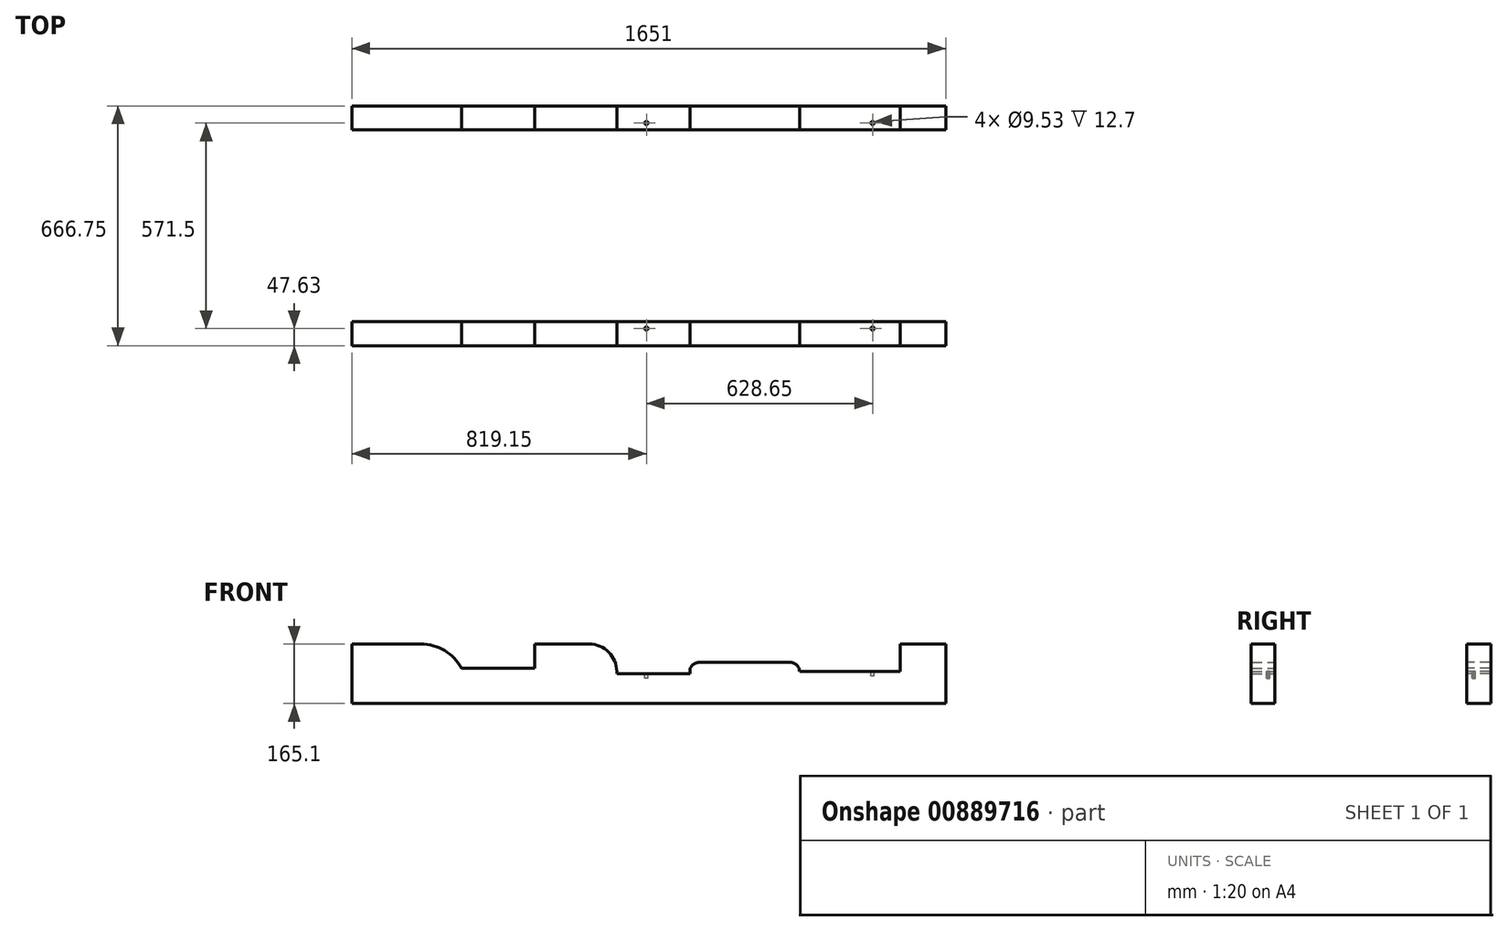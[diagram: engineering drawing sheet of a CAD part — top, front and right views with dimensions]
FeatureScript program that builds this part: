
annotation { "Feature Type Name" : "Feature", "Feature Type Description" : "" }
export const myFeature = defineFeature(function(context is Context, id is Id, definition is map)
    precondition{}
    {
        {
            var Q0;
            Q0=qCreatedBy(makeId("Front.planeOp"),FACE);
            var sketch = newSketch(context, id + "F0", { "sketchPlane" : qUnion([Q0])});
            skLineSegment(sketch, "E0", {"start": v(0, 0) * mm, "end": v(0, 165.1) * mm});
            skLineSegment(sketch, "E1", {"start": v(0, 165.1) * mm, "end": v(736.6, 165.1) * mm});
            skLineSegment(sketch, "E2", {"start": v(736.6, 165.1) * mm, "end": v(736.6, 82.55) * mm});
            skLineSegment(sketch, "E3", {"start": v(736.6, 82.55) * mm, "end": v(939.8, 82.55) * mm});
            skLineSegment(sketch, "E4", {"start": v(939.8, 82.55) * mm, "end": v(939.8, 114.3) * mm});
            skLineSegment(sketch, "E5", {"start": v(939.8, 114.3) * mm, "end": v(1244.6, 114.3) * mm});
            skLineSegment(sketch, "E6", {"start": v(1651, 165.1) * mm, "end": v(1651, 0) * mm});
            skLineSegment(sketch, "E7", {"start": v(1651, 0) * mm, "end": v(0, 0) * mm});
            skPoint(sketch, "E8.end.orphan", {"position": v(1244.6, 82.55) * mm});
            skLineSegment(sketch, "E9", {"start": v(1244.6, 114.3) * mm, "end": v(1244.6, 88.9) * mm});
            skLineSegment(sketch, "E10", {"start": v(1244.6, 88.9) * mm, "end": v(1524, 88.9) * mm});
            skLineSegment(sketch, "E11", {"start": v(1524, 88.9) * mm, "end": v(1524, 165.1) * mm});
            skLineSegment(sketch, "E12", {"start": v(1524, 165.1) * mm, "end": v(1651, 165.1) * mm});
            skSolve(sketch);
        }
        {
            var Q0;
            Q0=makeQuery(id+"F0.imprint","IMPRINT",FACE,{"disambiguationData":[TD([[makeQuery(id+"F0.imprint","IMPRINT",EDGE,{"derivedFrom":sQuery(id+"F0.wireOp",EDGE,"E0")}),-1.0]])]});
            extrude(context, id + "F1", {"entities" : qUnion([Q0]), "oppositeDirection" : true, "depth" : 66.67 * mm, "offsetDistance" : 25.4 * mm});
        }
        {
            var Q0;
            Q0=makeQuery(id+"F1.opExtrude","SWEPT_FACE",FACE,{"disambiguationData":[OSD([sQuery(id+"F0.wireOp",EDGE,"E3")])]});
            var sketch = newSketch(context, id + "F2", { "sketchPlane" : qUnion([Q0])});
            skLineSegment(sketch, "E13", {"start": v(736.6, 0) * mm, "end": v(819.15, 0) * mm, "construction": true});
            skLineSegment(sketch, "E14", {"start": v(819.15, 0) * mm, "end": v(819.15, 19.05) * mm, "construction": true});
            skCircle(sketch, "E15", {"center": v(819.15, 19.05) * mm, "radius": 4.76 * mm});
            skSolve(sketch);
        }
        {
            var Q0;
            Q0=makeQuery(id+"F2.imprint","IMPRINT",FACE,{"disambiguationData":[TD([[makeQuery(id+"F2.imprint","IMPRINT",EDGE,{"derivedFrom":sQuery(id+"F2.wireOp",EDGE,"E15")}),1.0]])]});
            extrude(context, id + "F3", {"entities" : qUnion([Q0]), "operationType" : NewBodyOperationType.REMOVE, "oppositeDirection" : true, "depth" : 12.7 * mm, "offsetDistance" : 25.4 * mm});
        }
        {
            var Q0;
            Q0=makeQuery(id+"F1.opExtrude","SWEPT_FACE",FACE,{"disambiguationData":[OSD([sQuery(id+"F0.wireOp",EDGE,"E10")])]});
            var sketch = newSketch(context, id + "F4", { "sketchPlane" : qUnion([Q0])});
            skLineSegment(sketch, "E16", {"start": v(1244.6, 0) * mm, "end": v(1447.8, 0) * mm, "construction": true});
            skLineSegment(sketch, "E17", {"start": v(1447.8, 0) * mm, "end": v(1447.8, 19.05) * mm, "construction": true});
            skCircle(sketch, "E18", {"center": v(1447.8, 19.05) * mm, "radius": 4.76 * mm});
            skSolve(sketch);
        }
        {
            var Q0;
            Q0 = qSketchRegion(id + "F4", true);
            extrude(context, id + "F5", {"entities" : qUnion([Q0]), "operationType" : NewBodyOperationType.REMOVE, "oppositeDirection" : true, "depth" : 12.7 * mm, "offsetDistance" : 25.4 * mm});
        }
        {
            var Q0;
            Q0=makeQuery(id+"F1.opExtrude","SWEPT_EDGE",EDGE,{"disambiguationData":[OSD([sQuery(id+"F0.wireOp",EDGE,"E1"),sQuery(id+"F0.wireOp",EDGE,"E2")])]});
            fillet(context, id + "F6", {"entities" : qUnion([Q0]), "radius" : 76.2 * mm, "tangentPropagation" : true, "allowEdgeOverflow" : false});
        }
        {
            var Q0;
            Q0=makeQuery(id+"F1.opExtrude","SWEPT_EDGE",EDGE,{"disambiguationData":[OSD([sQuery(id+"F0.wireOp",EDGE,"E4"),sQuery(id+"F0.wireOp",EDGE,"E5")])]});
            var Q1;
            Q1=makeQuery(id+"F1.opExtrude","SWEPT_EDGE",EDGE,{"disambiguationData":[OSD([sQuery(id+"F0.wireOp",EDGE,"E5"),sQuery(id+"F0.wireOp",EDGE,"E9")])]});
            fillet(context, id + "F7", {"entities" : qUnion([Q0, Q1]), "radius" : 25.4 * mm, "tangentPropagation" : true, "allowEdgeOverflow" : false});
        }
        {
            var Q0;
            Q0=makeQuery(id+"F1.opExtrude","CAP_FACE",FACE,{"disambiguationData":[OSD([sQuery(id+"F0.wireOp",EDGE,"E0"),sQuery(id+"F0.wireOp",EDGE,"E1"),sQuery(id+"F0.wireOp",EDGE,"E2"),sQuery(id+"F0.wireOp",EDGE,"E3"),sQuery(id+"F0.wireOp",EDGE,"E4"),sQuery(id+"F0.wireOp",EDGE,"E5"),sQuery(id+"F0.wireOp",EDGE,"E6"),sQuery(id+"F0.wireOp",EDGE,"E7"),sQuery(id+"F0.wireOp",EDGE,"E9"),sQuery(id+"F0.wireOp",EDGE,"E10"),sQuery(id+"F0.wireOp",EDGE,"E11"),sQuery(id+"F0.wireOp",EDGE,"E12")])],"isStart":true});
            cPlane(context, id + "F8", {"entities" : qUnion([Q0]), "cplaneType" : CPlaneType.OFFSET, "offset" : 266.7 * mm, "width" : 152.4 * mm, "height" : 152.4 * mm});
        }
        {
            var Q0;
            Q0=makeQuery(id+"F1.opExtrude","SWEPT_BODY",BODY,{"disambiguationData":[OSD([sQuery(id+"F0.wireOp",EDGE,"E0"),sQuery(id+"F0.wireOp",EDGE,"E1"),sQuery(id+"F0.wireOp",EDGE,"E2"),sQuery(id+"F0.wireOp",EDGE,"E3"),sQuery(id+"F0.wireOp",EDGE,"E4"),sQuery(id+"F0.wireOp",EDGE,"E5"),sQuery(id+"F0.wireOp",EDGE,"E6"),sQuery(id+"F0.wireOp",EDGE,"E7"),sQuery(id+"F0.wireOp",EDGE,"E9"),sQuery(id+"F0.wireOp",EDGE,"E10"),sQuery(id+"F0.wireOp",EDGE,"E11"),sQuery(id+"F0.wireOp",EDGE,"E12")])]});
            var Q1;
            Q1=qCreatedBy(id+"F8.planeOp",FACE);
            mirror(context, id + "F9", {"operationType" : NewBodyOperationType.ADD, "entities" : qUnion([Q0]), "mirrorPlane" : qUnion([Q1])});
        }
        {
            var Q0;
            Q0=makeQuery(id+"F1.opExtrude","CAP_FACE",FACE,{"disambiguationData":[OSD([sQuery(id+"F0.wireOp",EDGE,"E0"),sQuery(id+"F0.wireOp",EDGE,"E1"),sQuery(id+"F0.wireOp",EDGE,"E2"),sQuery(id+"F0.wireOp",EDGE,"E3"),sQuery(id+"F0.wireOp",EDGE,"E4"),sQuery(id+"F0.wireOp",EDGE,"E5"),sQuery(id+"F0.wireOp",EDGE,"E6"),sQuery(id+"F0.wireOp",EDGE,"E7"),sQuery(id+"F0.wireOp",EDGE,"E9"),sQuery(id+"F0.wireOp",EDGE,"E10"),sQuery(id+"F0.wireOp",EDGE,"E11"),sQuery(id+"F0.wireOp",EDGE,"E12")])],"isStart":true});
            var sketch = newSketch(context, id + "F10", { "sketchPlane" : qUnion([Q0])});
            skLineSegment(sketch, "E19", {"start": v(0, 165.1) * mm, "end": v(304.8, 165.1) * mm, "construction": true});
            skLineSegment(sketch, "E20", {"start": v(304.8, 165.1) * mm, "end": v(304.8, 98.42) * mm});
            skLineSegment(sketch, "E21", {"start": v(304.8, 98.42) * mm, "end": v(508, 98.43) * mm});
            skLineSegment(sketch, "E22", {"start": v(508, 98.43) * mm, "end": v(508, 165.1) * mm});
            skSolve(sketch);
        }
        {
            var Q0;
            {var subQ0=sQuery(id+"F10.wireOp",EDGE,"E20");Q0=makeQuery(id+"F10.imprint","IMPRINT",FACE,{"disambiguationData":[TD([[makeQuery(id+"F10.imprint","IMPRINT",EDGE,{"derivedFrom":subQ0}),1.0]])]});}
            extrude(context, id + "F11", {"entities" : qUnion([Q0]), "operationType" : NewBodyOperationType.REMOVE, "endBound" : BoundingType.THROUGH_ALL, "oppositeDirection" : true, "depth" : 25.4 * mm, "offsetDistance" : 25.4 * mm});
        }
        {
            var Q0;
            Q0=makeQuery(id+"F11.boolean.opBoolean","COPY",EDGE,{"derivedFrom":makeQuery(id+"F11.opExtrude","SWEPT_EDGE",EDGE,{"disambiguationData":[OSD([sQuery(id+"F0.wireOp",EDGE,"E1"),sQuery(id+"F10.wireOp",EDGE,"E20")])]})});
            var Q1;
            Q1=makeQuery(id+"F11.boolean.opBoolean","COPY",EDGE,{"derivedFrom":makeQuery(id+"F11.opExtrude","SWEPT_EDGE",EDGE,{"disambiguationData":[OSD([sQuery(id+"F0.wireOp",EDGE,"E1"),sQuery(id+"F10.wireOp",EDGE,"E22")])]})});
            fillet(context, id + "F12", {"entities" : qUnion([Q0, Q1]), "radius" : 127 * mm, "tangentPropagation" : true, "allowEdgeOverflow" : false});
        }
        {
            var Q0;
            Q0=makeQuery(id+"F9.opPattern","COPY",BODY,{"derivedFrom":makeQuery(id+"F1.opExtrude","SWEPT_BODY",BODY,{"disambiguationData":[OSD([sQuery(id+"F0.wireOp",EDGE,"E0"),sQuery(id+"F0.wireOp",EDGE,"E1"),sQuery(id+"F0.wireOp",EDGE,"E2"),sQuery(id+"F0.wireOp",EDGE,"E3"),sQuery(id+"F0.wireOp",EDGE,"E4"),sQuery(id+"F0.wireOp",EDGE,"E5"),sQuery(id+"F0.wireOp",EDGE,"E6"),sQuery(id+"F0.wireOp",EDGE,"E7"),sQuery(id+"F0.wireOp",EDGE,"E9"),sQuery(id+"F0.wireOp",EDGE,"E10"),sQuery(id+"F0.wireOp",EDGE,"E11"),sQuery(id+"F0.wireOp",EDGE,"E12")])]}),"instanceName":"1"});
            deleteBodies(context, id + "F13", {"entities" : qUnion([Q0])});
        }
        {
            var Q0;
            Q0=makeQuery(id+"F1.opExtrude","SWEPT_BODY",BODY,{"disambiguationData":[OSD([sQuery(id+"F0.wireOp",EDGE,"E0"),sQuery(id+"F0.wireOp",EDGE,"E1"),sQuery(id+"F0.wireOp",EDGE,"E2"),sQuery(id+"F0.wireOp",EDGE,"E3"),sQuery(id+"F0.wireOp",EDGE,"E4"),sQuery(id+"F0.wireOp",EDGE,"E5"),sQuery(id+"F0.wireOp",EDGE,"E6"),sQuery(id+"F0.wireOp",EDGE,"E7"),sQuery(id+"F0.wireOp",EDGE,"E9"),sQuery(id+"F0.wireOp",EDGE,"E10"),sQuery(id+"F0.wireOp",EDGE,"E11"),sQuery(id+"F0.wireOp",EDGE,"E12")])]});
            var Q1;
            Q1=qCreatedBy(id+"F8.planeOp",FACE);
            mirror(context, id + "F14", {"entities" : qUnion([Q0]), "mirrorPlane" : qUnion([Q1])});
        }
        {
            var Q0;
            Q0=makeQuery(id+"F14.opPattern","COPY",BODY,{"derivedFrom":makeQuery(id+"F1.opExtrude","SWEPT_BODY",BODY,{"disambiguationData":[OSD([sQuery(id+"F0.wireOp",EDGE,"E0"),sQuery(id+"F0.wireOp",EDGE,"E1"),sQuery(id+"F0.wireOp",EDGE,"E2"),sQuery(id+"F0.wireOp",EDGE,"E3"),sQuery(id+"F0.wireOp",EDGE,"E4"),sQuery(id+"F0.wireOp",EDGE,"E5"),sQuery(id+"F0.wireOp",EDGE,"E6"),sQuery(id+"F0.wireOp",EDGE,"E7"),sQuery(id+"F0.wireOp",EDGE,"E9"),sQuery(id+"F0.wireOp",EDGE,"E10"),sQuery(id+"F0.wireOp",EDGE,"E11"),sQuery(id+"F0.wireOp",EDGE,"E12")])]}),"instanceName":"1"});
            deleteBodies(context, id + "F15", {"entities" : qUnion([Q0])});
        }
        {
            var Q0;
            Q0=makeQuery(id+"F1.opExtrude","SWEPT_BODY",BODY,{"disambiguationData":[OSD([sQuery(id+"F0.wireOp",EDGE,"E0"),sQuery(id+"F0.wireOp",EDGE,"E1"),sQuery(id+"F0.wireOp",EDGE,"E2"),sQuery(id+"F0.wireOp",EDGE,"E3"),sQuery(id+"F0.wireOp",EDGE,"E4"),sQuery(id+"F0.wireOp",EDGE,"E5"),sQuery(id+"F0.wireOp",EDGE,"E6"),sQuery(id+"F0.wireOp",EDGE,"E7"),sQuery(id+"F0.wireOp",EDGE,"E9"),sQuery(id+"F0.wireOp",EDGE,"E10"),sQuery(id+"F0.wireOp",EDGE,"E11"),sQuery(id+"F0.wireOp",EDGE,"E12")])]});
            var Q1;
            Q1=qCreatedBy(id+"F8.planeOp",FACE);
            mirror(context, id + "F16", {"entities" : qUnion([Q0]), "mirrorPlane" : qUnion([Q1])});
        }
    });
